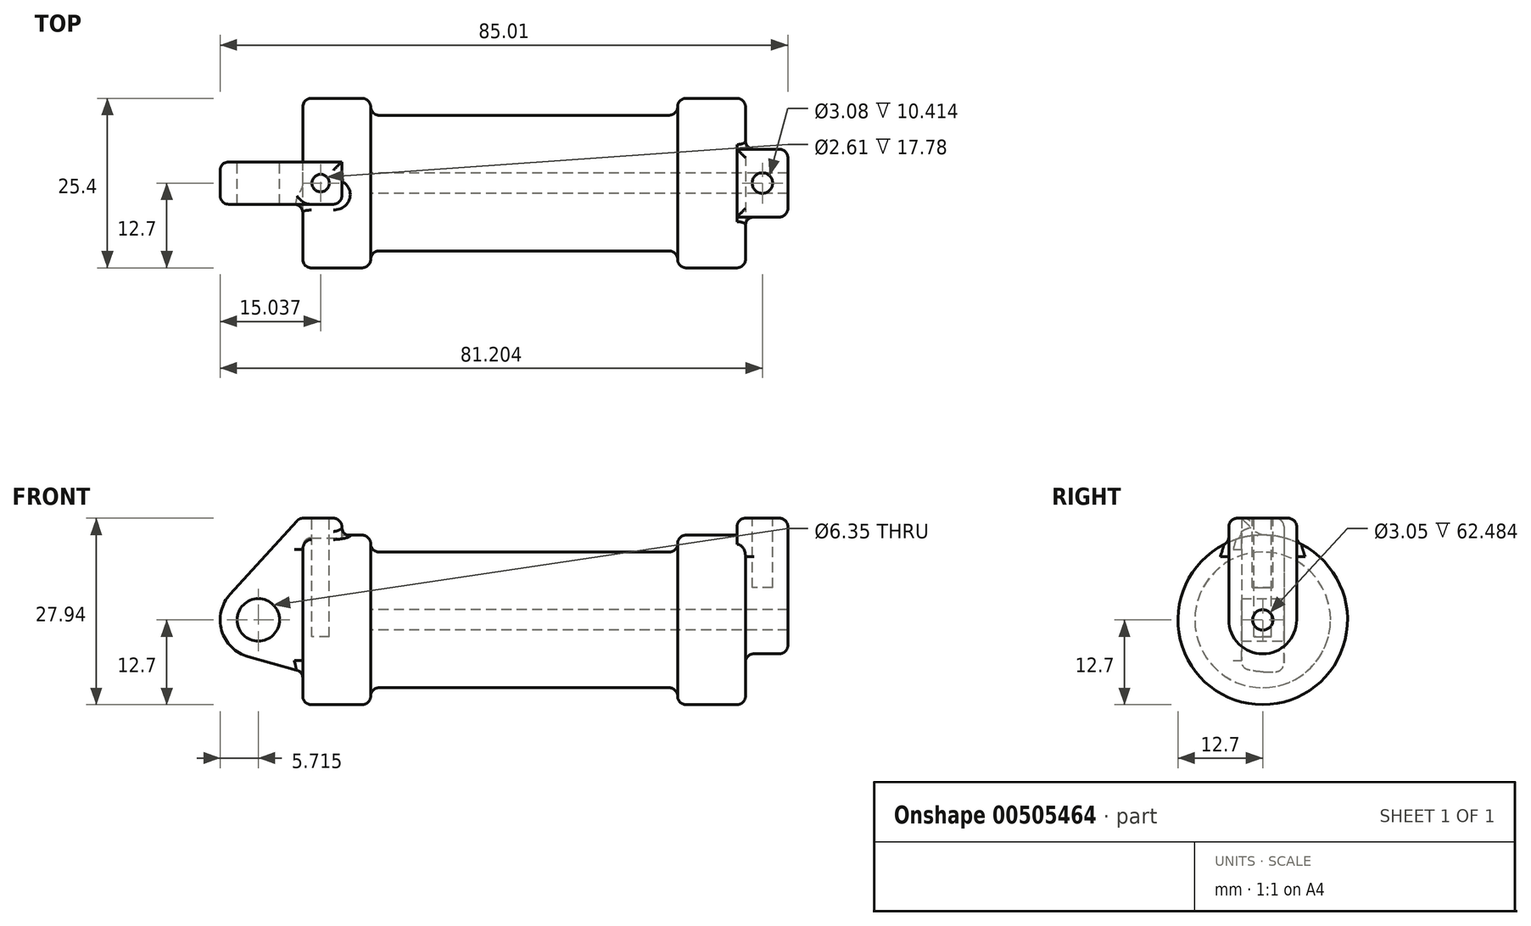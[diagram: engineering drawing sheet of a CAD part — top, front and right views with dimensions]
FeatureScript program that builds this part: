
annotation { "Feature Type Name" : "Feature", "Feature Type Description" : "" }
export const myFeature = defineFeature(function(context is Context, id is Id, definition is map)
    precondition{}
    {
        {
            var Q0;
            Q0=qCreatedBy(makeId("Front.planeOp"),FACE);
            var sketch = newSketch(context, id + "F0", { "sketchPlane" : qUnion([Q0])});
            skLineSegment(sketch, "E0", {"start": v(0, 0) * mm, "end": v(0, 12.7) * mm});
            skLineSegment(sketch, "E1", {"start": v(0, 12.7) * mm, "end": v(10.16, 12.7) * mm});
            skLineSegment(sketch, "E2", {"start": v(10.16, 12.7) * mm, "end": v(10.16, 10.16) * mm});
            skLineSegment(sketch, "E3", {"start": v(10.16, 10.16) * mm, "end": v(56.13, 10.16) * mm});
            skLineSegment(sketch, "E4", {"start": v(56.13, 10.16) * mm, "end": v(56.13, 12.7) * mm});
            skLineSegment(sketch, "E5", {"start": v(56.13, 12.7) * mm, "end": v(66.3, 12.7) * mm});
            skLineSegment(sketch, "E6", {"start": v(66.3, 12.7) * mm, "end": v(66.3, 0) * mm});
            skLineSegment(sketch, "E7", {"start": v(66.3, 0) * mm, "end": v(0, 0) * mm});
            skLineSegment(sketch, "E8", {"start": v(5.84, 15.24) * mm, "end": v(-0.5, 15.24) * mm});
            skLineSegment(sketch, "E9", {"start": v(-0.5, 15.24) * mm, "end": v(-10.88, 3.85) * mm});
            skLineSegment(sketch, "E10", {"start": v(0, 0) * mm, "end": v(-6.65, 0) * mm});
            skCircle(sketch, "E11", {"center": v(-6.65, 0) * mm, "radius": 5.72 * mm});
            skCircle(sketch, "E12", {"center": v(-6.65, 0) * mm, "radius": 3.18 * mm});
            skLineSegment(sketch, "E13", {"start": v(5.84, 15.24) * mm, "end": v(5.84, -9.4) * mm});
            skLineSegment(sketch, "E14", {"start": v(5.84, -9.4) * mm, "end": v(-8.18, -5.5) * mm});
            skSolve(sketch);
        }
        {
            var Q0;
            {var subQ0=sQuery(id+"F0.wireOp",EDGE,"E2");Q0=makeQuery(id+"F0.imprint","IMPRINT",FACE,{"disambiguationData":[TD([[makeQuery(id+"F0.imprint","IMPRINT",EDGE,{"derivedFrom":subQ0}),-1.0]])]});}
            var Q1;
            {var subQ0=sQuery(id+"F0.wireOp",EDGE,"E0");Q1=makeQuery(id+"F0.imprint","IMPRINT",FACE,{"disambiguationData":[TD([[makeQuery(id+"F0.imprint","IMPRINT",EDGE,{"derivedFrom":subQ0}),-1.0]])]});}
            var Q2;
            Q2=sQuery(id+"F0.wireOp",EDGE,"E7");
            revolve(context, id + "F1", {"entities" : qUnion([Q0, Q1]), "axis" : qUnion([Q2]), "revolveType" : RevolveType.FULL});
        }
        {
            var Q0;
            {var subQ0=sQuery(id+"F0.wireOp",EDGE,"E14");Q0=makeQuery(id+"F0.imprint","IMPRINT",FACE,{"disambiguationData":[TD([[makeQuery(id+"F0.imprint","IMPRINT",EDGE,{"derivedFrom":subQ0}),-1.0]])]});}
            var Q1;
            {var subQ0=sQuery(id+"F0.wireOp",EDGE,"E0");Q1=makeQuery(id+"F0.imprint","IMPRINT",FACE,{"disambiguationData":[TD([[makeQuery(id+"F0.imprint","IMPRINT",EDGE,{"derivedFrom":subQ0}),-1.0]])]});}
            var Q2;
            {var subQ1=sQuery(id+"F0.wireOp",EDGE,"E0");Q2=makeQuery(id+"F0.imprint","IMPRINT",FACE,{"disambiguationData":[TD([[makeQuery(id+"F0.imprint","IMPRINT",EDGE,{"derivedFrom":subQ1}),1.0]])]});}
            var Q3;
            {var subQ5=sQuery(id+"F0.wireOp",EDGE,"E12");Q3=makeQuery(id+"F0.imprint","IMPRINT",FACE,{"disambiguationData":[TD([[makeQuery(id+"F0.imprint","IMPRINT",EDGE,{"derivedFrom":subQ5}),-1.0]])]});}
            extrude(context, id + "F2", {"entities" : qUnion([Q0, Q1, Q2, Q3]), "operationType" : NewBodyOperationType.ADD, "endBound" : BoundingType.SYMMETRIC, "depth" : 6.35 * mm});
        }
        {
            var Q0;
            Q0=makeQuery(id+"F1.opRevolve","SWEPT_FACE",FACE,{"disambiguationData":[OSD([sQuery(id+"F0.wireOp",EDGE,"E6")])]});
            var sketch = newSketch(context, id + "F3", { "sketchPlane" : qUnion([Q0])});
            skCircle(sketch, "E15", {"center": v(0, 0) * mm, "radius": 1.52 * mm});
            skCircle(sketch, "E16", {"center": v(0, 0) * mm, "radius": 5.08 * mm});
            skLineSegment(sketch, "E17", {"start": v(-5.08, 0) * mm, "end": v(-5.08, 15.24) * mm});
            skLineSegment(sketch, "E18", {"start": v(-5.08, 15.24) * mm, "end": v(5.08, 15.24) * mm});
            skLineSegment(sketch, "E19", {"start": v(5.08, 15.24) * mm, "end": v(5.08, 0) * mm});
            skSolve(sketch);
        }
        {
            var Q0;
            {var subQ0=sQuery(id+"F3.wireOp",EDGE,"E17");var subQ1=sQuery(id+"F3.wireOp",EDGE,"E16");var subQ2=makeQuery(id+"F3.imprint","INTERSECT",VERTEX,{"derivedFrom":[subQ1,subQ0]});Q0=makeQuery(id+"F3.imprint","IMPRINT",FACE,{"disambiguationData":[TD([[makeQuery(id+"F3.imprint","IMPRINT",EDGE,{"disambiguationData":[TD([[subQ2,1.0]])],"derivedFrom":subQ1}),-1.0]])]});}
            var Q1;
            {var subQ0=sQuery(id+"F3.wireOp",EDGE,"E18");Q1=makeQuery(id+"F3.imprint","IMPRINT",FACE,{"disambiguationData":[TD([[makeQuery(id+"F3.imprint","IMPRINT",EDGE,{"derivedFrom":subQ0}),-1.0]])]});}
            var Q2;
            Q2=makeQuery(id+"F3.imprint","IMPRINT",FACE,{"disambiguationData":[TD([[makeQuery(id+"F3.imprint","IMPRINT",EDGE,{"derivedFrom":sQuery(id+"F3.wireOp",EDGE,"E15")}),-1.0]])]});
            extrude(context, id + "F4", {"entities" : qUnion([Q0, Q1, Q2]), "operationType" : NewBodyOperationType.ADD, "oppositeDirection" : true, "depth" : 1.27 * mm});
        }
        {
            var Q0;
            {var subQ0=sQuery(id+"F3.wireOp",EDGE,"E17");var subQ1=sQuery(id+"F3.wireOp",EDGE,"E16");var subQ2=makeQuery(id+"F3.imprint","INTERSECT",VERTEX,{"derivedFrom":[subQ1,subQ0]});Q0=makeQuery(id+"F3.imprint","IMPRINT",FACE,{"disambiguationData":[TD([[makeQuery(id+"F3.imprint","IMPRINT",EDGE,{"disambiguationData":[TD([[subQ2,1.0]])],"derivedFrom":subQ1}),-1.0]])]});}
            var Q1;
            {var subQ0=sQuery(id+"F3.wireOp",EDGE,"E18");Q1=makeQuery(id+"F3.imprint","IMPRINT",FACE,{"disambiguationData":[TD([[makeQuery(id+"F3.imprint","IMPRINT",EDGE,{"derivedFrom":subQ0}),-1.0]])]});}
            var Q2;
            Q2=makeQuery(id+"F3.imprint","IMPRINT",FACE,{"disambiguationData":[TD([[makeQuery(id+"F3.imprint","IMPRINT",EDGE,{"derivedFrom":sQuery(id+"F3.wireOp",EDGE,"E15")}),-1.0]])]});
            extrude(context, id + "F5", {"entities" : qUnion([Q0, Q1, Q2]), "operationType" : NewBodyOperationType.ADD, "depth" : 6.35 * mm});
        }
        {
            var Q0;
            Q0=makeQuery(id+"F3.imprint","IMPRINT",FACE,{"disambiguationData":[TD([[makeQuery(id+"F3.imprint","IMPRINT",EDGE,{"derivedFrom":sQuery(id+"F3.wireOp",EDGE,"E15")}),1.0]])]});
            var Q1;
            Q1=sQuery(id+"F3.wireOp",EDGE,"E15");
            var Q2;
            Q2=makeQuery(id+"F1.opRevolve","SWEPT_FACE",FACE,{"disambiguationData":[OSD([sQuery(id+"F0.wireOp",EDGE,"E2")])]});
            extrude(context, id + "F6", {"entities" : qUnion([Q0]), "operationType" : NewBodyOperationType.REMOVE, "surfaceEntities" : qUnion([Q1]), "endBound" : BoundingType.UP_TO_SURFACE, "oppositeDirection" : true, "endBoundEntityFace" : qUnion([Q2]), "depth" : 25.4 * mm});
        }
        {
            var Q0;
            Q0=makeQuery(id+"F2.opExtrude","SWEPT_FACE",FACE,{"disambiguationData":[OSD([sQuery(id+"F0.wireOp",EDGE,"E8")])]});
            var sketch = newSketch(context, id + "F7", { "sketchPlane" : qUnion([Q0])});
            skCircle(sketch, "E20", {"center": v(2.67, 0) * mm, "radius": 1.3 * mm});
            skSolve(sketch);
        }
        {
            var Q0;
            {var subQ0=sQuery(id+"F3.wireOp",EDGE,"E18");Q0=makeQuery(id+"F5.boolean.opBoolean","MERGE",FACE,{"derivedFrom":[makeQuery(id+"F4.opExtrude","SWEPT_FACE",FACE,{"disambiguationData":[OSD([subQ0])]}),makeQuery(id+"F5.opExtrude","SWEPT_FACE",FACE,{"disambiguationData":[OSD([subQ0])]})]});}
            var sketch = newSketch(context, id + "F8", { "sketchPlane" : qUnion([Q0])});
            skCircle(sketch, "E21", {"center": v(68.83, 0) * mm, "radius": 1.54 * mm});
            skSolve(sketch);
        }
        {
            var Q0;
            Q0=makeQuery(id+"F8.imprint","IMPRINT",FACE,{"disambiguationData":[TD([[makeQuery(id+"F8.imprint","IMPRINT",EDGE,{"derivedFrom":sQuery(id+"F8.wireOp",EDGE,"E21")}),1.0]])]});
            var Q1;
            Q1=sQuery(id+"F8.wireOp",EDGE,"E21");
            extrude(context, id + "F9", {"entities" : qUnion([Q0]), "operationType" : NewBodyOperationType.REMOVE, "surfaceEntities" : qUnion([Q1]), "oppositeDirection" : true, "depth" : 10.4 * mm});
        }
        {
            var Q0;
            Q0=makeQuery(id+"F7.imprint","IMPRINT",FACE,{"disambiguationData":[TD([[makeQuery(id+"F7.imprint","IMPRINT",EDGE,{"derivedFrom":sQuery(id+"F7.wireOp",EDGE,"E20")}),1.0]])]});
            var Q1;
            Q1=sQuery(id+"F7.wireOp",EDGE,"E20");
            extrude(context, id + "F10", {"entities" : qUnion([Q0]), "operationType" : NewBodyOperationType.REMOVE, "surfaceEntities" : qUnion([Q1]), "oppositeDirection" : true, "depth" : 17.78 * mm});
        }
        {
            var Q0;
            Q0=makeQuery(id+"F1.opRevolve","SWEPT_EDGE",EDGE,{"disambiguationData":[OSD([sQuery(id+"F0.wireOp",EDGE,"E0"),sQuery(id+"F0.wireOp",EDGE,"E1")])]});
            var Q1;
            Q1=makeQuery(id+"F1.opRevolve","SWEPT_EDGE",EDGE,{"disambiguationData":[OSD([sQuery(id+"F0.wireOp",EDGE,"E1"),sQuery(id+"F0.wireOp",EDGE,"E2")])]});
            var Q2;
            Q2=makeQuery(id+"F1.opRevolve","SWEPT_EDGE",EDGE,{"disambiguationData":[OSD([sQuery(id+"F0.wireOp",EDGE,"E2"),sQuery(id+"F0.wireOp",EDGE,"E3")])]});
            var Q3;
            Q3=makeQuery(id+"F1.opRevolve","SWEPT_EDGE",EDGE,{"disambiguationData":[OSD([sQuery(id+"F0.wireOp",EDGE,"E4"),sQuery(id+"F0.wireOp",EDGE,"E5")])]});
            var Q4;
            Q4=makeQuery(id+"F1.opRevolve","SWEPT_EDGE",EDGE,{"disambiguationData":[OSD([sQuery(id+"F0.wireOp",EDGE,"E5"),sQuery(id+"F0.wireOp",EDGE,"E6")])]});
            var Q5;
            Q5=makeQuery(id+"F1.opRevolve","SWEPT_EDGE",EDGE,{"disambiguationData":[OSD([sQuery(id+"F0.wireOp",EDGE,"E3"),sQuery(id+"F0.wireOp",EDGE,"E4")])]});
            fillet(context, id + "F11", {"entities" : qUnion([Q0, Q1, Q2, Q3, Q4, Q5]), "radius" : 1.27 * mm, "tangentPropagation" : true, "allowEdgeOverflow" : false});
        }
        {
            var Q0;
            Q0=makeQuery(id+"F2.opExtrude","CAP_EDGE",EDGE,{"disambiguationData":[OSD([sQuery(id+"F0.wireOp",EDGE,"E14")])],"isStart":false});
            var Q1;
            Q1=makeQuery(id+"F2.boolean.opBoolean","INTERSECT",EDGE,{"derivedFrom":[makeQuery(id+"F1.opRevolve","SWEPT_FACE",FACE,{"disambiguationData":[OSD([sQuery(id+"F0.wireOp",EDGE,"E0")])]}),makeQuery(id+"F2.opExtrude","CAP_FACE",FACE,{"disambiguationData":[OSD([sQuery(id+"F0.wireOp",EDGE,"E8"),sQuery(id+"F0.wireOp",EDGE,"E9"),sQuery(id+"F0.wireOp",EDGE,"E11"),sQuery(id+"F0.wireOp",EDGE,"E12"),sQuery(id+"F0.wireOp",EDGE,"E13"),sQuery(id+"F0.wireOp",EDGE,"E14")])],"isStart":false})]});
            var Q2;
            Q2=makeQuery(id+"F2.opExtrude","CAP_EDGE",EDGE,{"disambiguationData":[OSD([sQuery(id+"F0.wireOp",EDGE,"E13")])],"isStart":false});
            var Q3;
            Q3=makeQuery(id+"F2.opExtrude","SWEPT_EDGE",EDGE,{"disambiguationData":[OSD([sQuery(id+"F0.wireOp",EDGE,"E8"),sQuery(id+"F0.wireOp",EDGE,"E13")])]});
            var Q4;
            Q4=makeQuery(id+"F2.opExtrude","CAP_EDGE",EDGE,{"disambiguationData":[OSD([sQuery(id+"F0.wireOp",EDGE,"E8")])],"isStart":true});
            var Q5;
            Q5=makeQuery(id+"F2.opExtrude","CAP_EDGE",EDGE,{"disambiguationData":[OSD([sQuery(id+"F0.wireOp",EDGE,"E9")])],"isStart":true});
            var Q6;
            Q6=makeQuery(id+"F2.opExtrude","SWEPT_EDGE",EDGE,{"disambiguationData":[OSD([sQuery(id+"F0.wireOp",EDGE,"E8"),sQuery(id+"F0.wireOp",EDGE,"E9")])]});
            fillet(context, id + "F12", {"entities" : qUnion([Q0, Q1, Q2, Q3, Q4, Q5, Q6]), "radius" : 1.27 * mm, "tangentPropagation" : true, "allowEdgeOverflow" : false});
        }
        {
            var Q0;
            Q0=makeQuery(id+"F5.opExtrude","CAP_EDGE",EDGE,{"disambiguationData":[OSD([sQuery(id+"F3.wireOp",EDGE,"E18")])],"isStart":false});
            var Q1;
            {var subQ0=sQuery(id+"F3.wireOp",EDGE,"E18");var subQ1=sQuery(id+"F3.wireOp",EDGE,"E17");Q1=makeQuery(id+"F5.boolean.opBoolean","MERGE",EDGE,{"derivedFrom":[makeQuery(id+"F4.opExtrude","SWEPT_EDGE",EDGE,{"disambiguationData":[OSD([subQ1,subQ0])]}),makeQuery(id+"F5.opExtrude","SWEPT_EDGE",EDGE,{"disambiguationData":[OSD([subQ1,subQ0])]})]});}
            var Q2;
            Q2=makeQuery(id+"F5.opExtrude","CAP_EDGE",EDGE,{"disambiguationData":[OSD([sQuery(id+"F3.wireOp",EDGE,"E16")])],"isStart":false});
            var Q3;
            {var subQ0=sQuery(id+"F3.wireOp",EDGE,"E17");Q3=makeQuery(id+"F11.opFillet","BLEND_EDGE",EDGE,{"blendedFrom":[makeQuery(id+"F1.opRevolve","SWEPT_EDGE",EDGE,{"disambiguationData":[OSD([sQuery(id+"F0.wireOp",EDGE,"E5"),sQuery(id+"F0.wireOp",EDGE,"E6")])]}),makeQuery(id+"F5.boolean.opBoolean","MERGE",FACE,{"derivedFrom":[makeQuery(id+"F4.opExtrude","SWEPT_FACE",FACE,{"disambiguationData":[OSD([subQ0])]}),makeQuery(id+"F5.opExtrude","SWEPT_FACE",FACE,{"disambiguationData":[OSD([subQ0])]})]})],"blendedInto":[makeQuery(id+"F5.boolean.opBoolean","MERGE",FACE,{"derivedFrom":[makeQuery(id+"F4.opExtrude","SWEPT_FACE",FACE,{"disambiguationData":[OSD([subQ0])]}),makeQuery(id+"F5.opExtrude","SWEPT_FACE",FACE,{"disambiguationData":[OSD([subQ0])]})]})]});}
            var Q4;
            {var subQ0=sQuery(id+"F3.wireOp",EDGE,"E19");var subQ1=sQuery(id+"F3.wireOp",EDGE,"E18");Q4=makeQuery(id+"F5.boolean.opBoolean","MERGE",EDGE,{"derivedFrom":[makeQuery(id+"F4.opExtrude","SWEPT_EDGE",EDGE,{"disambiguationData":[OSD([subQ1,subQ0])]}),makeQuery(id+"F5.opExtrude","SWEPT_EDGE",EDGE,{"disambiguationData":[OSD([subQ1,subQ0])]})]});}
            var Q5;
            Q5=makeQuery(id+"F4.opExtrude","CAP_EDGE",EDGE,{"disambiguationData":[OSD([sQuery(id+"F3.wireOp",EDGE,"E18")])],"isStart":false});
            fillet(context, id + "F13", {"entities" : qUnion([Q0, Q1, Q2, Q3, Q4, Q5]), "radius" : 1.27 * mm, "tangentPropagation" : true, "allowEdgeOverflow" : false});
        }
    });
